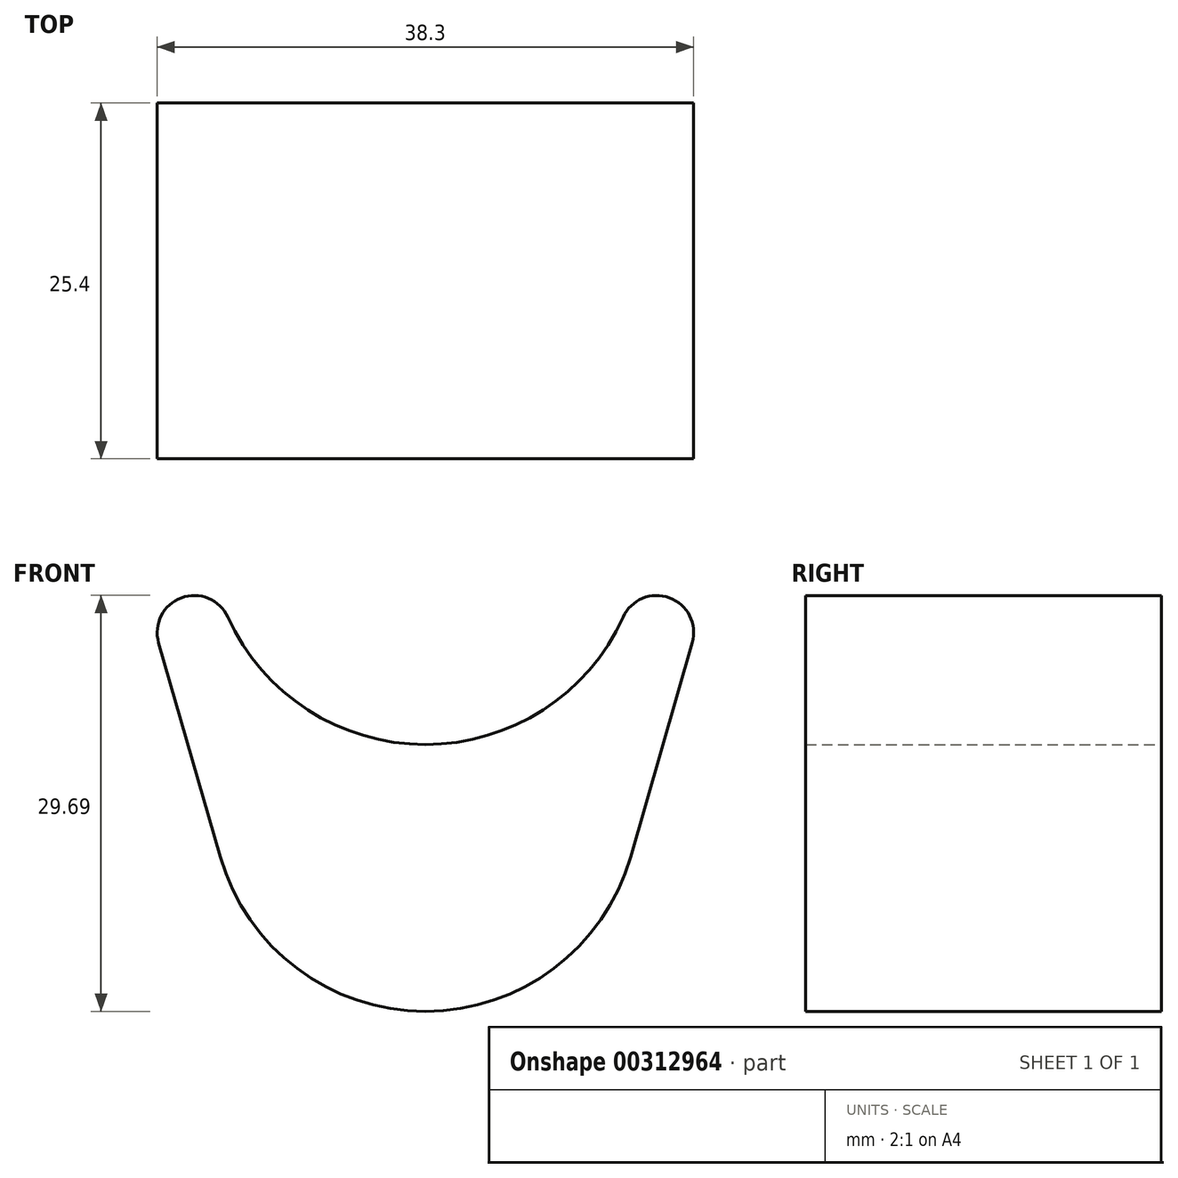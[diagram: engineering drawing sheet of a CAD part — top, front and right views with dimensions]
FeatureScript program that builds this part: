
annotation { "Feature Type Name" : "Feature", "Feature Type Description" : "" }
export const myFeature = defineFeature(function(context is Context, id is Id, definition is map)
    precondition{}
    {
        {
            var Q0;
            Q0=qCreatedBy(makeId("Front.planeOp"),FACE);
            var sketch = newSketch(context, id + "F0", { "sketchPlane" : qUnion([Q0])});
            skLineSegment(sketch, "E0", {"start": v(-14.9, -4.28) * mm, "end": v(-19.77, -5.68) * mm});
            skLineSegment(sketch, "E1", {"start": v(-19.77, -5.68) * mm, "end": v(-14.65, -23.52) * mm});
            skArc(sketch, "E2", {"start": v(-14.65, -23.52) * mm, "mid": v(0, -34.54) * mm, "end": v(14.65, -23.52) * mm});
            skLineSegment(sketch, "E3", {"start": v(0, 0) * mm, "end": v(0, -19.3) * mm, "construction": true});
            skLineSegment(sketch, "E4.MirrorCS", {"start": v(19.77, -5.68) * mm, "end": v(14.65, -23.52) * mm});
            skLineSegment(sketch, "E5.MirrorCS", {"start": v(14.9, -4.28) * mm, "end": v(19.77, -5.68) * mm});
            skArc(sketch, "E6", {"start": v(-14.9, -4.28) * mm, "mid": v(0, -15.5) * mm, "end": v(14.9, -4.28) * mm});
            skArc(sketch, "E7", {"start": v(-14.1, -6.4) * mm, "mid": v(-17.42, -5.02) * mm, "end": v(-19.04, -8.22) * mm});
            skArc(sketch, "E8.MirrorCS", {"start": v(14.1, -6.4) * mm, "mid": v(17.42, -5.02) * mm, "end": v(19.04, -8.22) * mm});
            skSolve(sketch);
        }
        {
            var Q0;
            {var subQ11=sQuery(id+"F0.wireOp",EDGE,"E2");Q0=makeQuery(id+"F0.imprint","IMPRINT",FACE,{"disambiguationData":[TD([[makeQuery(id+"F0.imprint","IMPRINT",EDGE,{"derivedFrom":subQ11}),1.0]])]});}
            extrude(context, id + "F1", {"entities" : qUnion([Q0]), "depth" : 25.4 * mm, "symmetric" : true});
        }
    });
